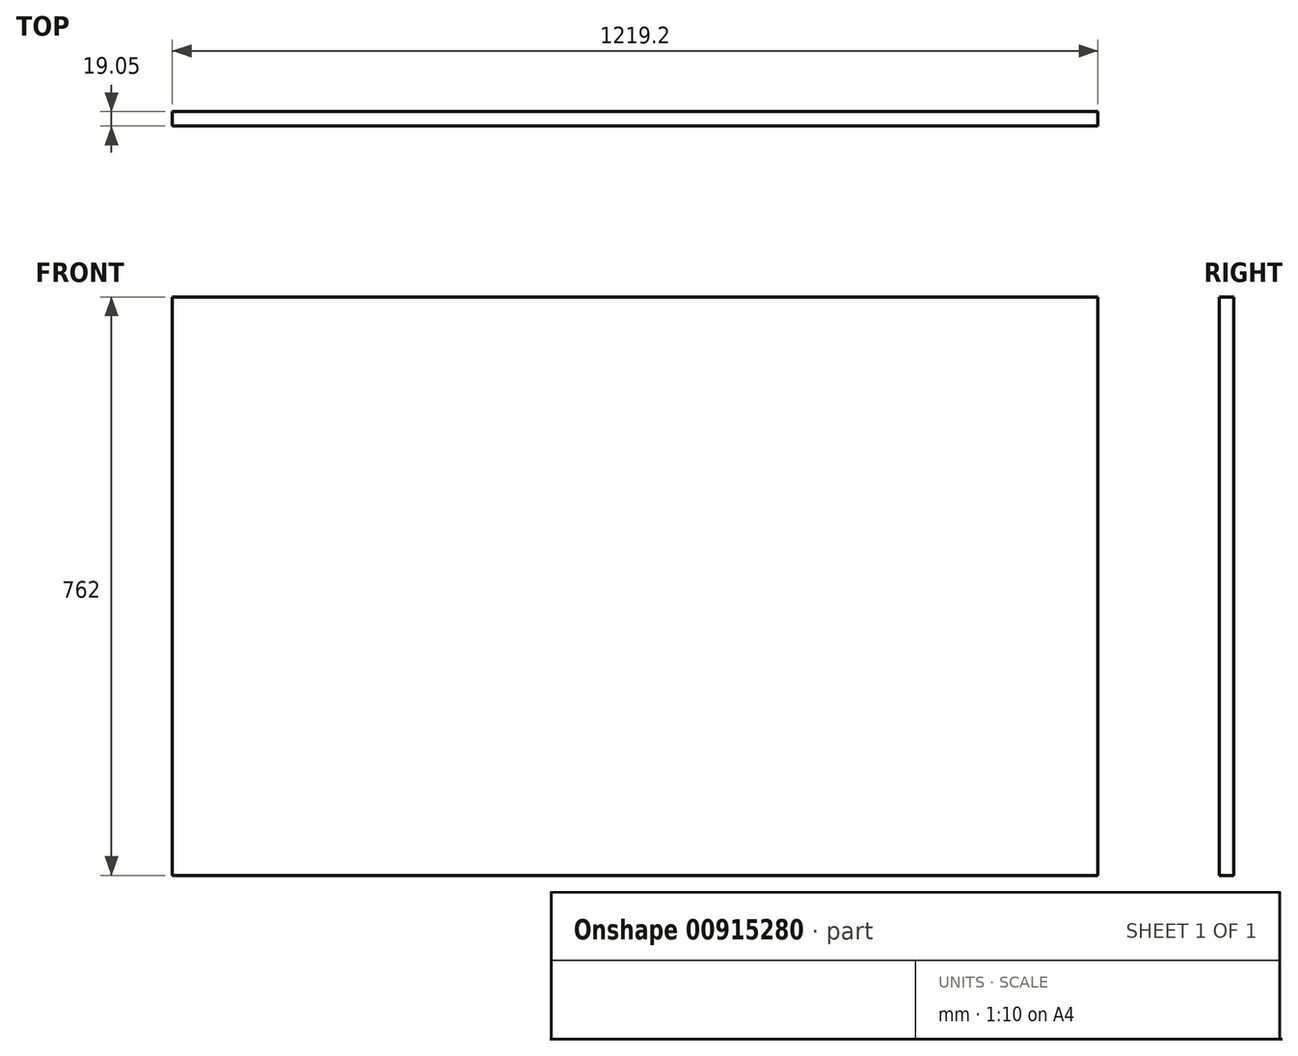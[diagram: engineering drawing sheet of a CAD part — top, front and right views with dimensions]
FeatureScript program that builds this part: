
annotation { "Feature Type Name" : "Feature", "Feature Type Description" : "" }
export const myFeature = defineFeature(function(context is Context, id is Id, definition is map)
    precondition{}
    {
        {
            var Q0;
            Q0=qCreatedBy(makeId("Front.planeOp"),FACE);
            var sketch = newSketch(context, id + "F0", { "sketchPlane" : qUnion([Q0])});
            skLineSegment(sketch, "E0.bottom", {"start": v(609.6, 381) * mm, "end": v(-609.6, 381) * mm});
            skLineSegment(sketch, "E0.top", {"start": v(609.6, -381) * mm, "end": v(-609.6, -381) * mm});
            skLineSegment(sketch, "E0.left", {"start": v(609.6, 381) * mm, "end": v(609.6, -381) * mm});
            skLineSegment(sketch, "E0.right", {"start": v(-609.6, 381) * mm, "end": v(-609.6, -381) * mm});
            skPoint(sketch, "E0.middle", {"position": v(0, 0) * mm});
            skSolve(sketch);
        }
        {
            var Q0;
            Q0=makeQuery(id+"F0.imprint","IMPRINT",FACE,{"disambiguationData":[TD([[makeQuery(id+"F0.imprint","IMPRINT",EDGE,{"derivedFrom":sQuery(id+"F0.wireOp",EDGE,"E0.bottom")}),1.0]])]});
            extrude(context, id + "F1", {"entities" : qUnion([Q0]), "depth" : 19.05 * mm, "offsetDistance" : 25.4 * mm});
        }
    });
